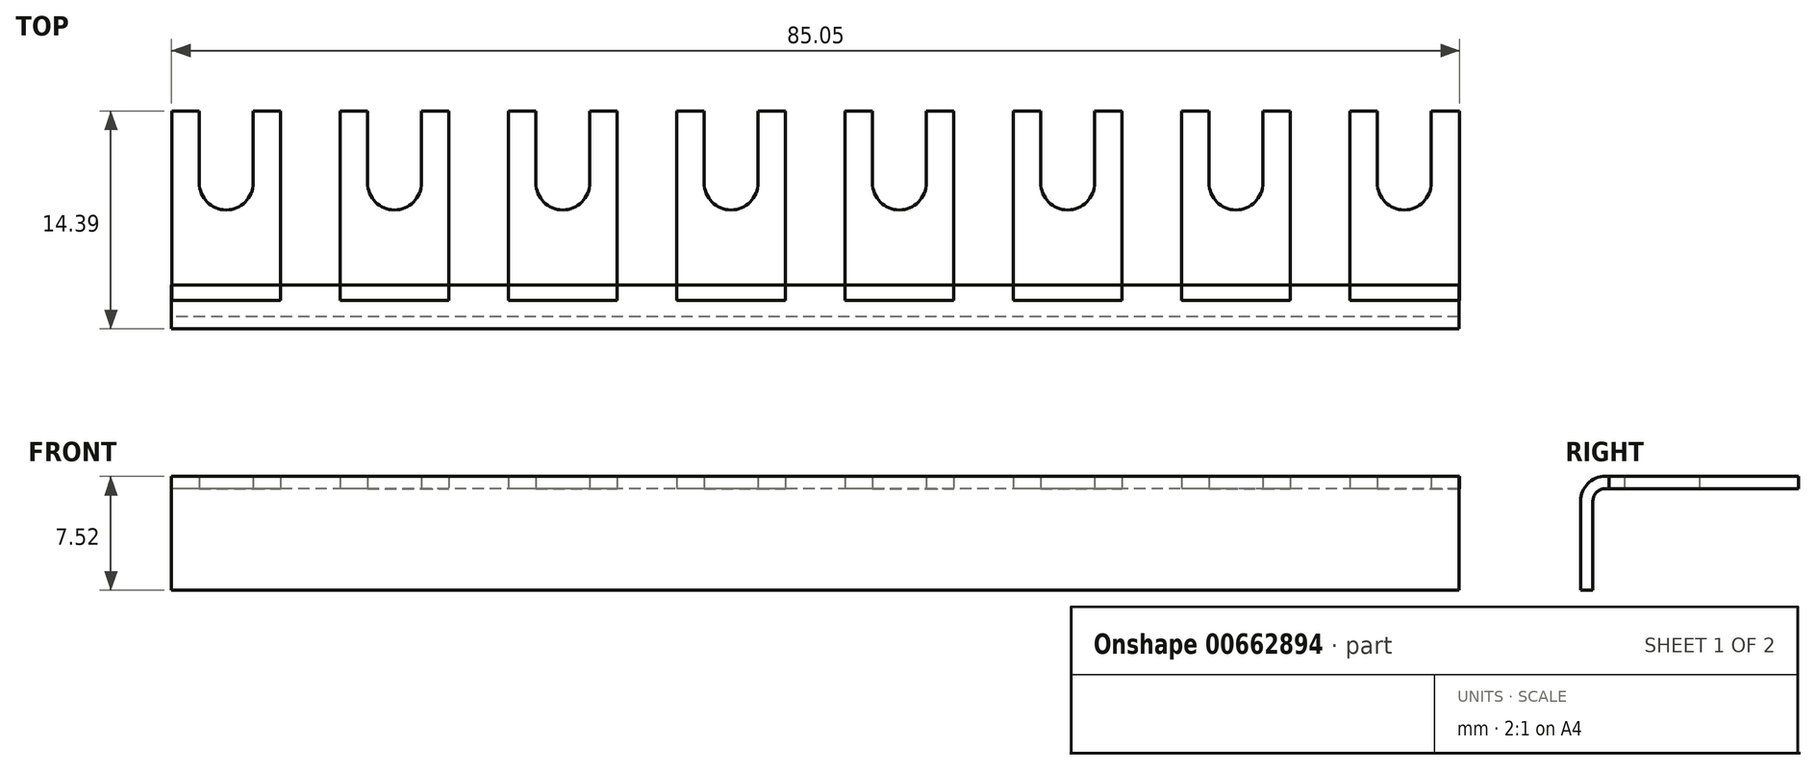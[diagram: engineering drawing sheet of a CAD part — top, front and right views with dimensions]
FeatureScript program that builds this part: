
annotation { "Feature Type Name" : "Feature", "Feature Type Description" : "" }
export const myFeature = defineFeature(function(context is Context, id is Id, definition is map)
    precondition{}
    {
        {
            var Q0;
            Q0=qCreatedBy(makeId("Top.planeOp"),FACE);
            var sketch = newSketch(context, id + "F0", { "sketchPlane" : qUnion([Q0])});
            skLineSegment(sketch, "E0.right", {"start": v(-42.48, 1.44) * mm, "end": v(-42.48, -11.09) * mm});
            skPoint(sketch, "E0.middle", {"position": v(0.03, -5.08) * mm});
            skPoint(sketch, "E1.endSnap0", {"position": v(0.03, 5.44) * mm});
            skLineSegment(sketch, "E2", {"start": v(-40.68, -3.31) * mm, "end": v(-40.68, 1.44) * mm});
            skLineSegment(sketch, "E3", {"start": v(-37.12, 1.44) * mm, "end": v(-37.12, -3.31) * mm});
            skLineSegment(sketch, "E4.trimOffspring", {"start": v(-40.68, 1.44) * mm, "end": v(-42.48, 1.44) * mm});
            skArc(sketch, "E5", {"start": v(-40.68, -3.31) * mm, "mid": v(-38.9, -5.1) * mm, "end": v(-37.12, -3.31) * mm});
            skLineSegment(sketch, "E6", {"start": v(-37.12, 1.44) * mm, "end": v(-35.32, 1.44) * mm});
            skLineSegment(sketch, "E7", {"start": v(-35.32, 1.44) * mm, "end": v(-35.32, -11.09) * mm});
            skLineSegment(sketch, "E8", {"start": v(-31.37, 1.44) * mm, "end": v(-31.37, -11.09) * mm});
            skLineSegment(sketch, "E9", {"start": v(-29.56, -3.31) * mm, "end": v(-29.56, 1.44) * mm});
            skLineSegment(sketch, "E10", {"start": v(-26, 1.44) * mm, "end": v(-26, -3.31) * mm});
            skLineSegment(sketch, "E11.trimOffspring", {"start": v(-29.56, 1.44) * mm, "end": v(-31.37, 1.44) * mm});
            skArc(sketch, "E12", {"start": v(-29.56, -3.31) * mm, "mid": v(-27.78, -5.1) * mm, "end": v(-26, -3.31) * mm});
            skLineSegment(sketch, "E13", {"start": v(-26, 1.44) * mm, "end": v(-24.2, 1.44) * mm});
            skLineSegment(sketch, "E14", {"start": v(-24.2, 1.44) * mm, "end": v(-24.2, -11.09) * mm});
            skLineSegment(sketch, "E15", {"start": v(-20.25, 1.44) * mm, "end": v(-20.25, -11.09) * mm});
            skLineSegment(sketch, "E16", {"start": v(-18.45, -3.31) * mm, "end": v(-18.45, 1.44) * mm});
            skLineSegment(sketch, "E17", {"start": v(-14.9, 1.44) * mm, "end": v(-14.9, -3.31) * mm});
            skLineSegment(sketch, "E18.trimOffspring", {"start": v(-18.45, 1.44) * mm, "end": v(-20.25, 1.44) * mm});
            skArc(sketch, "E19", {"start": v(-18.45, -3.31) * mm, "mid": v(-16.67, -5.1) * mm, "end": v(-14.9, -3.31) * mm});
            skLineSegment(sketch, "E20", {"start": v(-14.9, 1.44) * mm, "end": v(-13.1, 1.44) * mm});
            skLineSegment(sketch, "E21", {"start": v(-13.1, 1.44) * mm, "end": v(-13.1, -11.09) * mm});
            skLineSegment(sketch, "E22", {"start": v(-9.14, 1.44) * mm, "end": v(-9.14, -11.09) * mm});
            skLineSegment(sketch, "E23", {"start": v(-7.34, -3.31) * mm, "end": v(-7.34, 1.44) * mm});
            skLineSegment(sketch, "E24", {"start": v(-3.78, 1.44) * mm, "end": v(-3.78, -3.31) * mm});
            skLineSegment(sketch, "E25.trimOffspring", {"start": v(-7.34, 1.44) * mm, "end": v(-9.14, 1.44) * mm});
            skArc(sketch, "E26", {"start": v(-7.34, -3.31) * mm, "mid": v(-5.56, -5.1) * mm, "end": v(-3.78, -3.31) * mm});
            skLineSegment(sketch, "E27", {"start": v(-3.78, 1.44) * mm, "end": v(-1.98, 1.44) * mm});
            skLineSegment(sketch, "E28", {"start": v(-1.98, 1.44) * mm, "end": v(-1.98, -11.09) * mm});
            skLineSegment(sketch, "E29", {"start": v(1.97, 1.44) * mm, "end": v(1.97, -11.09) * mm});
            skLineSegment(sketch, "E30", {"start": v(3.77, -3.31) * mm, "end": v(3.77, 1.44) * mm});
            skLineSegment(sketch, "E31", {"start": v(7.33, 1.44) * mm, "end": v(7.33, -3.31) * mm});
            skLineSegment(sketch, "E32.trimOffspring", {"start": v(3.77, 1.44) * mm, "end": v(1.97, 1.44) * mm});
            skArc(sketch, "E33", {"start": v(3.77, -3.31) * mm, "mid": v(5.55, -5.1) * mm, "end": v(7.33, -3.31) * mm});
            skLineSegment(sketch, "E34", {"start": v(7.33, 1.44) * mm, "end": v(9.13, 1.44) * mm});
            skLineSegment(sketch, "E35", {"start": v(9.13, 1.44) * mm, "end": v(9.13, -11.09) * mm});
            skLineSegment(sketch, "E36", {"start": v(13.08, 1.44) * mm, "end": v(13.08, -11.09) * mm});
            skLineSegment(sketch, "E37", {"start": v(14.89, -3.31) * mm, "end": v(14.89, 1.44) * mm});
            skLineSegment(sketch, "E38", {"start": v(18.44, 1.44) * mm, "end": v(18.44, -3.31) * mm});
            skLineSegment(sketch, "E39.trimOffspring", {"start": v(14.89, 1.44) * mm, "end": v(13.08, 1.44) * mm});
            skArc(sketch, "E40", {"start": v(14.89, -3.31) * mm, "mid": v(16.67, -5.1) * mm, "end": v(18.44, -3.31) * mm});
            skLineSegment(sketch, "E41", {"start": v(18.44, 1.44) * mm, "end": v(20.25, 1.44) * mm});
            skLineSegment(sketch, "E42", {"start": v(20.25, 1.44) * mm, "end": v(20.25, -11.09) * mm});
            skLineSegment(sketch, "E43", {"start": v(24.2, 1.44) * mm, "end": v(24.2, -11.09) * mm});
            skLineSegment(sketch, "E44", {"start": v(26, -3.31) * mm, "end": v(26, 1.44) * mm});
            skLineSegment(sketch, "E45", {"start": v(29.56, 1.44) * mm, "end": v(29.56, -3.31) * mm});
            skLineSegment(sketch, "E46.trimOffspring", {"start": v(26, 1.44) * mm, "end": v(24.2, 1.44) * mm});
            skArc(sketch, "E47", {"start": v(26, -3.31) * mm, "mid": v(27.78, -5.1) * mm, "end": v(29.56, -3.31) * mm});
            skLineSegment(sketch, "E48", {"start": v(29.56, 1.44) * mm, "end": v(31.36, 1.44) * mm});
            skLineSegment(sketch, "E49", {"start": v(31.36, 1.44) * mm, "end": v(31.36, -11.09) * mm});
            skLineSegment(sketch, "E50", {"start": v(35.3, 1.44) * mm, "end": v(35.3, -11.09) * mm});
            skLineSegment(sketch, "E51", {"start": v(37.11, -3.31) * mm, "end": v(37.11, 1.44) * mm});
            skLineSegment(sketch, "E52", {"start": v(40.67, 1.44) * mm, "end": v(40.67, -3.31) * mm});
            skLineSegment(sketch, "E53.trimOffspring", {"start": v(37.11, 1.44) * mm, "end": v(35.3, 1.44) * mm});
            skArc(sketch, "E54", {"start": v(37.11, -3.31) * mm, "mid": v(38.9, -5.1) * mm, "end": v(40.67, -3.31) * mm});
            skLineSegment(sketch, "E55", {"start": v(40.67, 1.44) * mm, "end": v(42.54, 1.44) * mm});
            skLineSegment(sketch, "E56", {"start": v(42.54, -11.09) * mm, "end": v(42.54, 1.44) * mm});
            skPoint(sketch, "E57.startSnap0", {"position": v(-38.9, -5.1) * mm});
            skLineSegment(sketch, "E58", {"start": v(42.54, -11.09) * mm, "end": v(-42.48, -11.09) * mm});
            skPoint(sketch, "E59.orphan", {"position": v(-42.48, -11.34) * mm});
            skSolve(sketch);
        }
        {
            var Q0;
            Q0=qCreatedBy(makeId("Right.planeOp"),FACE);
            var sketch = newSketch(context, id + "F1", { "sketchPlane" : qUnion([Q0])});
            skArc(sketch, "E60", {"start": v(-11.33, 0) * mm, "mid": v(-11.9, -0.24) * mm, "end": v(-12.14, -0.81) * mm});
            skLineSegment(sketch, "E61", {"start": v(-12.14, -0.81) * mm, "end": v(-12.14, -6.7) * mm});
            skPoint(sketch, "E62.start.orphan", {"position": v(-5.66, 0) * mm});
            skLineSegment(sketch, "E63.0", {"start": v(-12.95, -0.81) * mm, "end": v(-12.95, -6.7) * mm});
            skArc(sketch, "E63.1", {"start": v(-11.33, 0.81) * mm, "mid": v(-12.48, 0.34) * mm, "end": v(-12.95, -0.81) * mm});
            skLineSegment(sketch, "E63.2", {"start": v(-10.06, 0.81) * mm, "end": v(-11.33, 0.81) * mm});
            skLineSegment(sketch, "E64", {"start": v(-12.95, -6.7) * mm, "end": v(-12.14, -6.7) * mm});
            skLineSegment(sketch, "E65", {"start": v(-10.06, 0.81) * mm, "end": v(-10.06, 0) * mm});
            skLineSegment(sketch, "E66.trimOffspring", {"start": v(-10.06, 0) * mm, "end": v(-11.33, 0) * mm});
            skPoint(sketch, "E67.start.orphan", {"position": v(0, 0) * mm});
            skSolve(sketch);
        }
        {
            var Q0;
            Q0 = qSketchRegion(id + "F0", true);
            extrude(context, id + "F2", {"entities" : qUnion([Q0]), "depth" : 0.81 * mm, "offsetDistance" : 25.4 * mm});
        }
        {
            var Q0;
            Q0 = qSketchRegion(id + "F1", true);
            extrude(context, id + "F3", {"entities" : qUnion([Q0]), "endBound" : BoundingType.SYMMETRIC, "depth" : 85.01 * mm, "offsetDistance" : 25.4 * mm});
        }
    });
